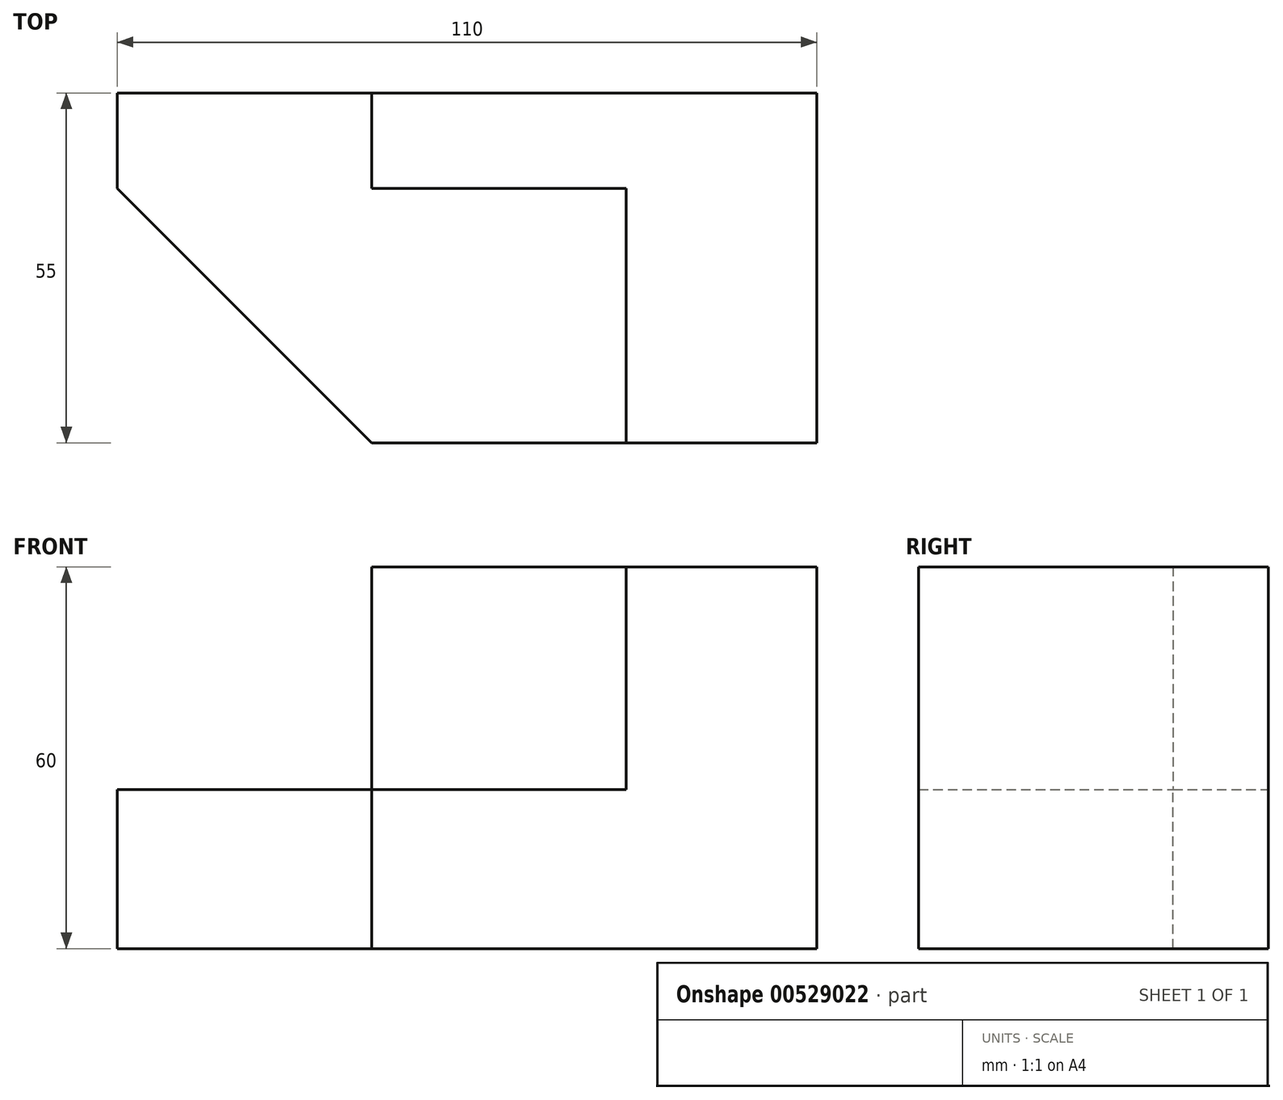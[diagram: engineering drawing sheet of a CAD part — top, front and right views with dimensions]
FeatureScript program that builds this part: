
annotation { "Feature Type Name" : "Feature", "Feature Type Description" : "" }
export const myFeature = defineFeature(function(context is Context, id is Id, definition is map)
    precondition{}
    {
        {
            var Q0;
            Q0=qCreatedBy(makeId("Front.planeOp"),FACE);
            var sketch = newSketch(context, id + "F0", { "sketchPlane" : qUnion([Q0])});
            skLineSegment(sketch, "E0", {"start": v(-49.05, 0) * mm, "end": v(60.95, 0) * mm});
            skLineSegment(sketch, "E1", {"start": v(60.95, 0) * mm, "end": v(60.95, 60) * mm});
            skLineSegment(sketch, "E2", {"start": v(60.95, 60) * mm, "end": v(30.95, 60) * mm});
            skLineSegment(sketch, "E3", {"start": v(30.95, 60) * mm, "end": v(30.95, 25) * mm});
            skLineSegment(sketch, "E4", {"start": v(30.95, 25) * mm, "end": v(-9.05, 25) * mm});
            skLineSegment(sketch, "E5", {"start": v(-49.05, 0) * mm, "end": v(-49.05, 25) * mm});
            skLineSegment(sketch, "E6", {"start": v(-49.05, 25) * mm, "end": v(-9.05, 25) * mm});
            skLineSegment(sketch, "E7", {"start": v(-9.05, 25) * mm, "end": v(-9.05, 60) * mm});
            skLineSegment(sketch, "E8", {"start": v(-9.05, 60) * mm, "end": v(30.95, 60) * mm});
            skLineSegment(sketch, "E9", {"start": v(-9.05, 0) * mm, "end": v(60.95, 0) * mm});
            skSolve(sketch);
        }
        {
            var Q0;
            Q0=makeQuery(id+"F0.imprint","IMPRINT",FACE,{"disambiguationData":[TD([[makeQuery(id+"F0.imprint","IMPRINT",EDGE,{"derivedFrom":sQuery(id+"F0.wireOp",EDGE,"E1")}),1.0]])]});
            extrude(context, id + "F1", {"entities" : qUnion([Q0]), "depth" : 55 * mm, "offsetDistance" : 25 * mm});
        }
        {
            var Q0;
            Q0 = qSketchRegion(id + "F0", true);
            extrude(context, id + "F2", {"entities" : qUnion([Q0]), "operationType" : NewBodyOperationType.ADD, "depth" : 15 * mm, "offsetDistance" : 25 * mm});
        }
        {
            var Q0;
            Q0=makeQuery(id+"F1.opExtrude","CAP_EDGE",EDGE,{"disambiguationData":[OSD([sQuery(id+"F0.wireOp",EDGE,"E5")])],"isStart":false});
            chamfer(context, id + "F3", {"entities" : qUnion([Q0]), "width" : 40 * mm, "tangentPropagation" : true});
        }
    });
